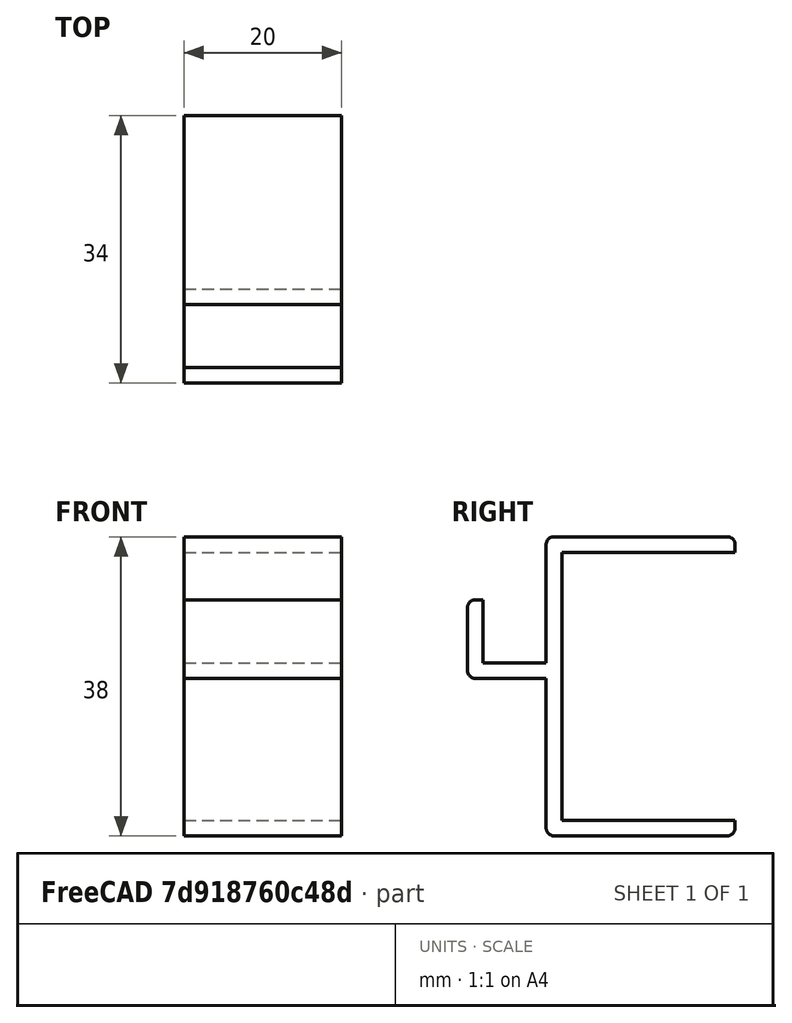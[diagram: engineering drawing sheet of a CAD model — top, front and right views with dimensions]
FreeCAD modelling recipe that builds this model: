
FCSTD DOCUMENT  (FreeCAD 0.16R6712 (Git))
Label: monitor-arm-hanger
License: All rights reserved
LicenseURL: http://en.wikipedia.org/wiki/All_rights_reserved
objects: Part::Box×4, Part::Cut×2, Part::MultiFuse×1, Part::Fillet×1
note: 8 computed .brp shape members not serialized (recipe doc carries the construction recipe); baked Part::Feature solids carry a one-line shape summary decoded from their .brp

FEATURE [Part::Box] Box  label="Cube"
  Height = 38
  Length = 20
  Width = 24
FEATURE [Part::Box] Box001  label="Cube001"
  Height = 34
  Length = 20
  Placement = pos=(0,2,2) rot=(0,0,1;0rad)
  Width = 30
FEATURE [Part::Cut] Cut
  Base = -> Box
  Tool = -> Box001
FEATURE [Part::Box] Box002  label="Cube002"
  Height = 8
  Length = 20
  Placement = pos=(0,-8,22) rot=(0,0,1;0rad)
  Width = 8
FEATURE [Part::Box] Box003  label="Cube003"
  Height = 10
  Length = 20
  Placement = pos=(0,-10,20) rot=(0,0,1;0rad)
  Width = 10
FEATURE [Part::Cut] Cut001
  Base = -> Box003
  Tool = -> Box002
FEATURE [Part::MultiFuse] Fusion
  Shapes = -> [Cut001,Cut]
FEATURE [Part::Fillet] Fillet
  Base = -> Fusion
  Edges = 6 edges r=1: [Edge4,Edge16,Edge37,Edge38,Edge39,Edge44]
